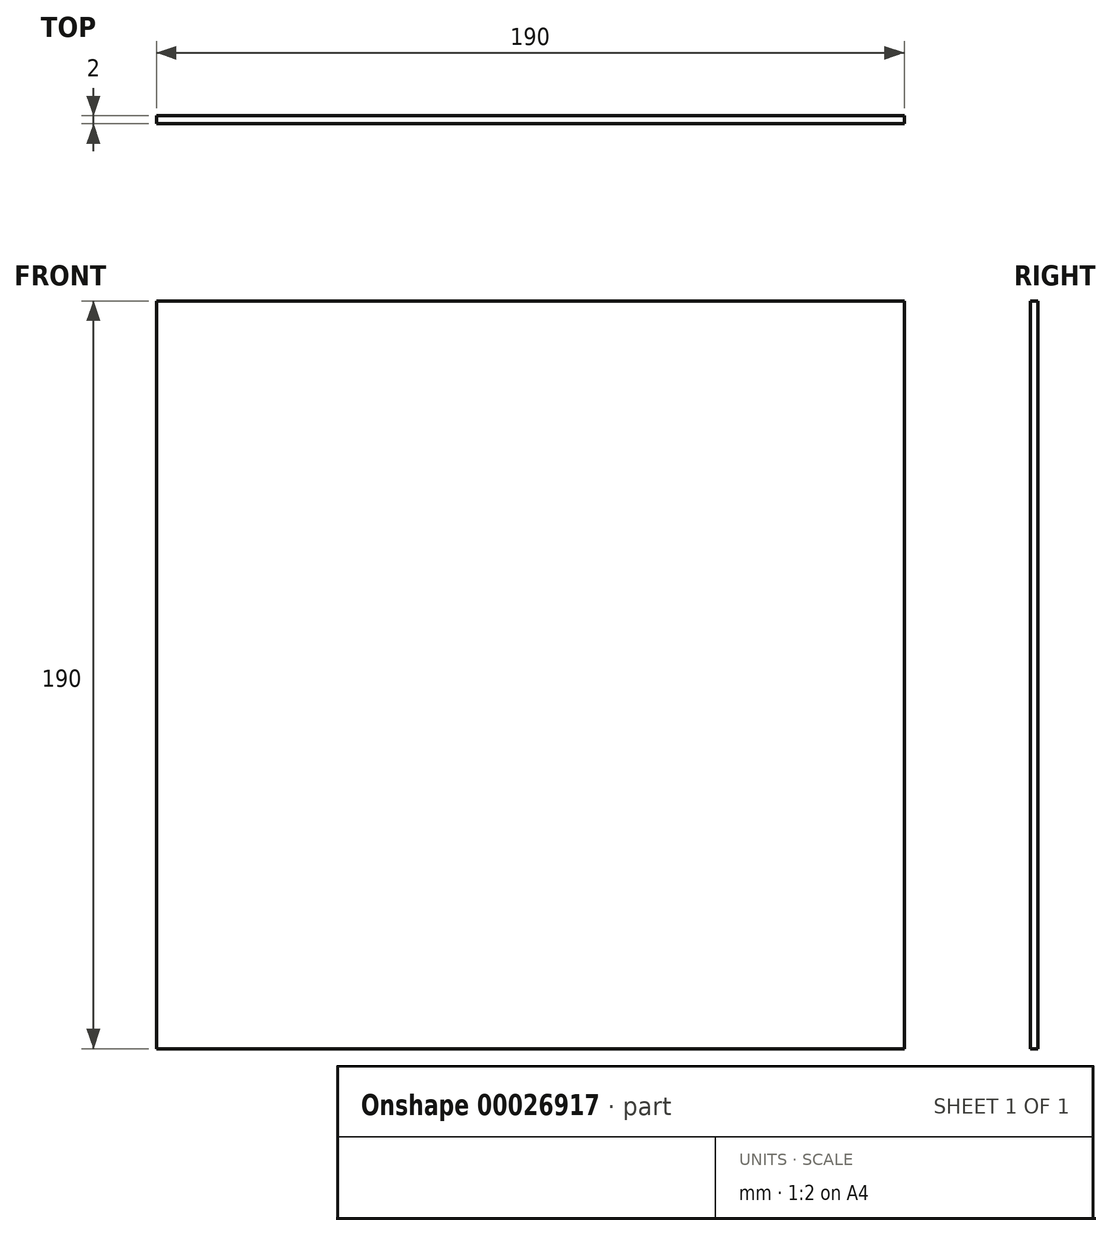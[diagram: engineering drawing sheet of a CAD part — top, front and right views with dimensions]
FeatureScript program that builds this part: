
annotation { "Feature Type Name" : "Feature", "Feature Type Description" : "" }
export const myFeature = defineFeature(function(context is Context, id is Id, definition is map)
    precondition{}
    {
        {
            var Q0;
            Q0=qCreatedBy(makeId("Front.planeOp"),FACE);
            var sketch = newSketch(context, id + "F0", { "sketchPlane" : qUnion([Q0])});
            skLineSegment(sketch, "E0.bottom", {"start": v(-95, 95) * mm, "end": v(95, 95) * mm});
            skLineSegment(sketch, "E0.top", {"start": v(-95, -95) * mm, "end": v(95, -95) * mm});
            skLineSegment(sketch, "E0.left", {"start": v(-95, 95) * mm, "end": v(-95, -95) * mm});
            skLineSegment(sketch, "E0.right", {"start": v(95, 95) * mm, "end": v(95, -95) * mm});
            skSolve(sketch);
        }
        {
            var Q0;
            Q0=qSketchRegion(id+"F0",true);
            extrude(context, id + "F1", {"entities" : qUnion([Q0]), "depth" : 2 * mm});
        }
    });
